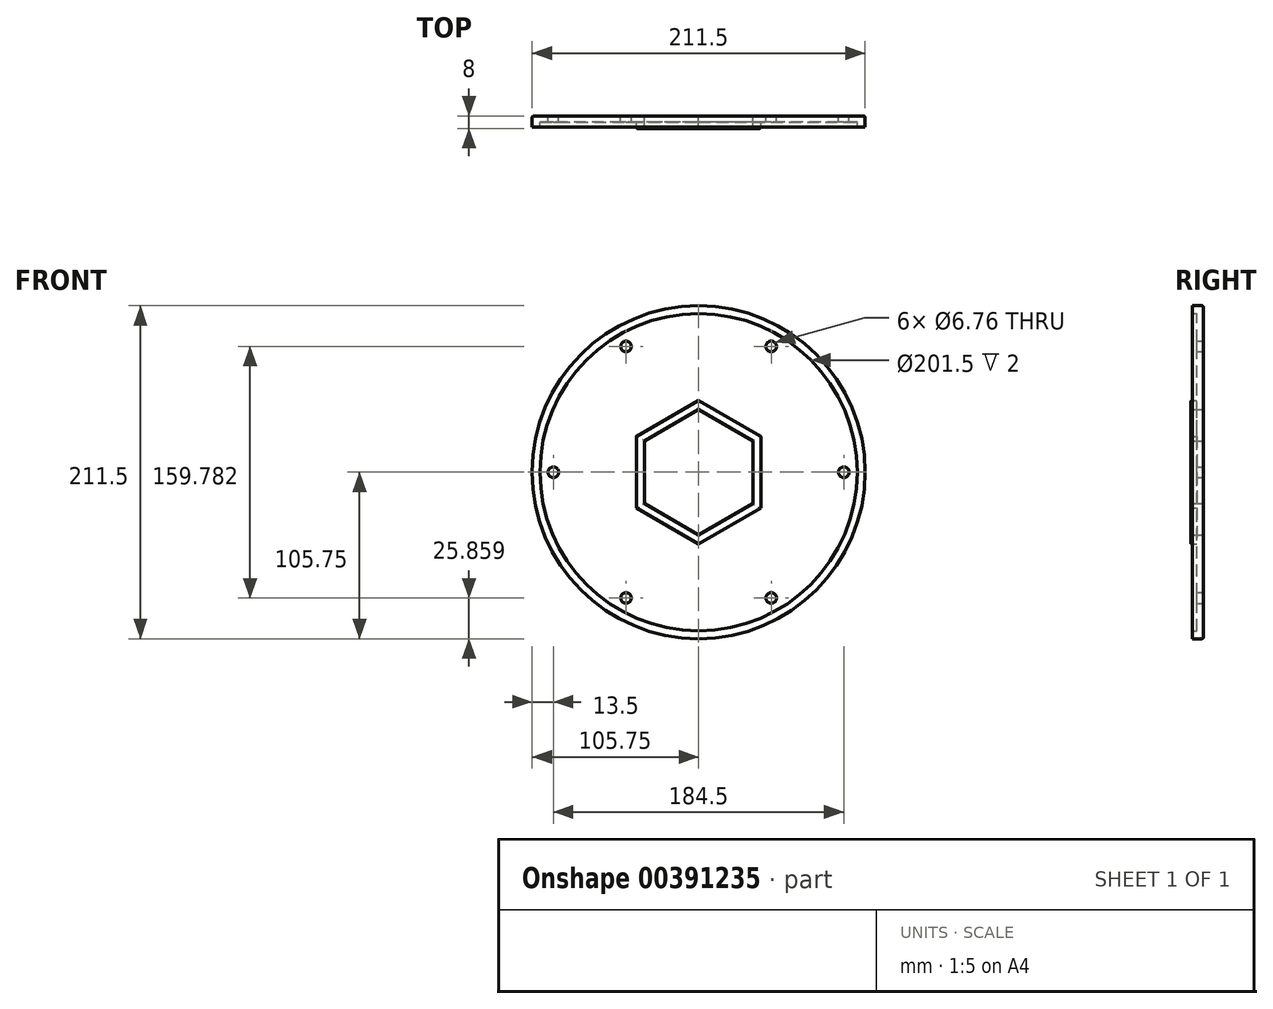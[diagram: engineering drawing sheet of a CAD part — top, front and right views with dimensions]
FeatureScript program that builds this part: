
annotation { "Feature Type Name" : "Feature", "Feature Type Description" : "" }
export const myFeature = defineFeature(function(context is Context, id is Id, definition is map)
    precondition{}
    {
        {
            var Q0;
            Q0=qCreatedBy(makeId("Front.planeOp"),FACE);
            var sketch = newSketch(context, id + "F0", { "sketchPlane" : qUnion([Q0])});
            skCircle(sketch, "E0.cCircle", {"center": v(0, 0) * mm, "radius": 80.5 * mm, "construction": true});
            skLineSegment(sketch, "E0.0", {"start": v(80.5, -46.48) * mm, "end": v(0, -92.95) * mm});
            skLineSegment(sketch, "E0.1", {"start": v(0, -92.95) * mm, "end": v(-80.5, -46.48) * mm});
            skLineSegment(sketch, "E0.2", {"start": v(-80.5, -46.48) * mm, "end": v(-80.5, 46.48) * mm});
            skLineSegment(sketch, "E0.3", {"start": v(-80.5, 46.48) * mm, "end": v(0, 92.95) * mm});
            skLineSegment(sketch, "E0.4", {"start": v(0, 92.95) * mm, "end": v(80.5, 46.48) * mm});
            skLineSegment(sketch, "E0.5", {"start": v(80.5, 46.48) * mm, "end": v(80.5, -46.48) * mm});
            skPoint(sketch, "E0.0.midPoint", {"position": v(40.25, -69.72) * mm});
            skPoint(sketch, "E1.0.midPoint", {"position": v(83.75, 0) * mm});
            skCircle(sketch, "E2", {"center": v(0, 0) * mm, "radius": 100.75 * mm});
            skPoint(sketch, "E3.0.midPoint", {"position": v(19.75, -35.93) * mm});
            skCircle(sketch, "E4.cCircle", {"center": v(0, 0) * mm, "radius": 34.5 * mm, "construction": true});
            skLineSegment(sketch, "E4.0", {"start": v(34.5, -19.92) * mm, "end": v(0, -39.84) * mm});
            skLineSegment(sketch, "E4.1", {"start": v(0, -39.84) * mm, "end": v(-34.5, -19.92) * mm});
            skLineSegment(sketch, "E4.2", {"start": v(-34.5, -19.92) * mm, "end": v(-34.5, 19.92) * mm});
            skLineSegment(sketch, "E4.3", {"start": v(-34.5, 19.92) * mm, "end": v(0, 39.84) * mm});
            skLineSegment(sketch, "E4.4", {"start": v(0, 39.84) * mm, "end": v(34.5, 19.92) * mm});
            skLineSegment(sketch, "E4.5", {"start": v(34.5, 19.92) * mm, "end": v(34.5, -19.92) * mm});
            skPoint(sketch, "E4.0.midPoint", {"position": v(17.25, -29.88) * mm});
            skPoint(sketch, "E5.visualSharp", {"position": v(0, 96.7) * mm});
            skPoint(sketch, "E6.visualSharp", {"position": v(83.75, 48.35) * mm});
            skPoint(sketch, "E7.visualSharp", {"position": v(83.75, -48.35) * mm});
            skPoint(sketch, "E8.visualSharp", {"position": v(0, -96.7) * mm});
            skPoint(sketch, "E9.visualSharp", {"position": v(-83.75, -48.35) * mm});
            skPoint(sketch, "E10.visualSharp", {"position": v(-83.75, 48.35) * mm});
            skPoint(sketch, "E11.visualSharp", {"position": v(39.66, 22.9) * mm});
            skPoint(sketch, "E12.visualSharp", {"position": v(39.58, -24.48) * mm});
            skPoint(sketch, "E13.visualSharp", {"position": v(-0.08, -47.38) * mm});
            skPoint(sketch, "E14.visualSharp", {"position": v(-39.66, -22.9) * mm});
            skPoint(sketch, "E15.visualSharp", {"position": v(-39.66, 22.9) * mm});
            skPoint(sketch, "E16.visualSharp", {"position": v(0, 45.8) * mm});
            skCircle(sketch, "E17.cCircle", {"center": v(0, 0) * mm, "radius": 77.5 * mm, "construction": true});
            skLineSegment(sketch, "E17.0", {"start": v(77.5, 44.74) * mm, "end": v(77.5, -44.74) * mm});
            skLineSegment(sketch, "E17.1", {"start": v(77.5, -44.74) * mm, "end": v(0, -89.49) * mm});
            skLineSegment(sketch, "E17.2", {"start": v(0, -89.49) * mm, "end": v(-77.5, -44.74) * mm});
            skLineSegment(sketch, "E17.3", {"start": v(-77.5, -44.74) * mm, "end": v(-77.5, 44.74) * mm});
            skLineSegment(sketch, "E17.4", {"start": v(-77.5, 44.74) * mm, "end": v(0, 89.49) * mm});
            skLineSegment(sketch, "E17.5", {"start": v(0, 89.49) * mm, "end": v(77.5, 44.74) * mm});
            skPoint(sketch, "E17.0.midPoint", {"position": v(77.5, 0) * mm});
            skCircle(sketch, "E18.cCircle", {"center": v(0, 0) * mm, "radius": 39.5 * mm, "construction": true});
            skLineSegment(sketch, "E18.0", {"start": v(39.5, -22.8) * mm, "end": v(0, -45.61) * mm});
            skLineSegment(sketch, "E18.1", {"start": v(0, -45.61) * mm, "end": v(-39.5, -22.8) * mm});
            skLineSegment(sketch, "E18.2", {"start": v(-39.5, -22.8) * mm, "end": v(-39.5, 22.8) * mm});
            skLineSegment(sketch, "E18.3", {"start": v(-39.5, 22.8) * mm, "end": v(0, 45.61) * mm});
            skLineSegment(sketch, "E18.4", {"start": v(0, 45.61) * mm, "end": v(39.5, 22.8) * mm});
            skLineSegment(sketch, "E18.5", {"start": v(39.5, 22.8) * mm, "end": v(39.5, -22.8) * mm});
            skPoint(sketch, "E18.0.midPoint", {"position": v(19.75, -34.2) * mm});
            skCircle(sketch, "E19", {"center": v(0, 0) * mm, "radius": 105.75 * mm});
            skPoint(sketch, "E20", {"position": v(-46.12, 79.9) * mm});
            skPoint(sketch, "E21", {"position": v(46.12, 79.9) * mm});
            skPoint(sketch, "E22", {"position": v(92.25, 0) * mm});
            skPoint(sketch, "E23", {"position": v(46.13, -79.9) * mm});
            skPoint(sketch, "E24", {"position": v(-46.12, -79.9) * mm});
            skPoint(sketch, "E25", {"position": v(-92.25, 0) * mm});
            skSolve(sketch);
        }
        {
            var Q0;
            Q0=makeQuery(id+"F0.imprint","IMPRINT",FACE,{"disambiguationData":[TD([[makeQuery(id+"F0.imprint","IMPRINT",EDGE,{"derivedFrom":sQuery(id+"F0.wireOp",EDGE,"E0.0")}),1.0]])]});
            var Q1;
            Q1=makeQuery(id+"F0.imprint","IMPRINT",FACE,{"disambiguationData":[TD([[makeQuery(id+"F0.imprint","IMPRINT",EDGE,{"derivedFrom":sQuery(id+"F0.wireOp",EDGE,"E17.0")}),-1.0]])]});
            extrude(context, id + "F1", {"entities" : qUnion([Q0, Q1]), "depth" : 4 * mm});
        }
        {
            var Q0;
            Q0=makeQuery(id+"F0.imprint","IMPRINT",FACE,{"disambiguationData":[TD([[makeQuery(id+"F0.imprint","IMPRINT",EDGE,{"derivedFrom":sQuery(id+"F0.wireOp",EDGE,"E0.0")}),-1.0]])]});
            extrude(context, id + "F2", {"entities" : qUnion([Q0]), "depth" : 4 * mm});
        }
        {
            var Q0;
            Q0=makeQuery(id+"F0.imprint","IMPRINT",FACE,{"disambiguationData":[TD([[makeQuery(id+"F0.imprint","IMPRINT",EDGE,{"derivedFrom":sQuery(id+"F0.wireOp",EDGE,"E4.0")}),1.0]])]});
            extrude(context, id + "F3", {"entities" : qUnion([Q0]), "operationType" : NewBodyOperationType.ADD, "depth" : 8 * mm});
        }
        {
            var Q0;
            Q0=makeQuery(id+"F0.imprint","IMPRINT",FACE,{"disambiguationData":[TD([[makeQuery(id+"F0.imprint","IMPRINT",EDGE,{"derivedFrom":sQuery(id+"F0.wireOp",EDGE,"E2")}),-1.0]])]});
            extrude(context, id + "F4", {"entities" : qUnion([Q0]), "operationType" : NewBodyOperationType.ADD, "depth" : 7 * mm});
        }
        {
            var Q0;
            Q0=makeQuery(id+"F1.opExtrude","SWEPT_BODY",BODY,{"disambiguationData":[OSD([sQuery(id+"F0.wireOp",EDGE,"E0.0"),sQuery(id+"F0.wireOp",EDGE,"E0.1"),sQuery(id+"F0.wireOp",EDGE,"E0.2"),sQuery(id+"F0.wireOp",EDGE,"E0.3"),sQuery(id+"F0.wireOp",EDGE,"E0.4"),sQuery(id+"F0.wireOp",EDGE,"E0.5"),sQuery(id+"F0.wireOp",EDGE,"E2")])]});
            var Q1;
            Q1=makeQuery(id+"F1.opExtrude","SWEPT_BODY",BODY,{"disambiguationData":[OSD([sQuery(id+"F0.wireOp",EDGE,"E17.0"),sQuery(id+"F0.wireOp",EDGE,"E17.1"),sQuery(id+"F0.wireOp",EDGE,"E17.2"),sQuery(id+"F0.wireOp",EDGE,"E17.3"),sQuery(id+"F0.wireOp",EDGE,"E17.4"),sQuery(id+"F0.wireOp",EDGE,"E17.5"),sQuery(id+"F0.wireOp",EDGE,"E18.0"),sQuery(id+"F0.wireOp",EDGE,"E18.1"),sQuery(id+"F0.wireOp",EDGE,"E18.2"),sQuery(id+"F0.wireOp",EDGE,"E18.3"),sQuery(id+"F0.wireOp",EDGE,"E18.4"),sQuery(id+"F0.wireOp",EDGE,"E18.5")])]});
            var Q2;
            Q2=makeQuery(id+"F2.opExtrude","SWEPT_BODY",BODY,{"disambiguationData":[OSD([sQuery(id+"F0.wireOp",EDGE,"E0.0"),sQuery(id+"F0.wireOp",EDGE,"E0.1"),sQuery(id+"F0.wireOp",EDGE,"E0.2"),sQuery(id+"F0.wireOp",EDGE,"E0.3"),sQuery(id+"F0.wireOp",EDGE,"E0.4"),sQuery(id+"F0.wireOp",EDGE,"E0.5"),sQuery(id+"F0.wireOp",EDGE,"E17.0"),sQuery(id+"F0.wireOp",EDGE,"E17.1"),sQuery(id+"F0.wireOp",EDGE,"E17.2"),sQuery(id+"F0.wireOp",EDGE,"E17.3"),sQuery(id+"F0.wireOp",EDGE,"E17.4"),sQuery(id+"F0.wireOp",EDGE,"E17.5")])]});
            booleanBodies(context, id + "F5", {"operationType" : BooleanOperationType.UNION, "tools" : qUnion([Q0, Q1, Q2])});
        }
        {
            var Q0;
            Q0=makeQuery(id+"F3.opExtrude","CAP_EDGE",EDGE,{"disambiguationData":[OSD([sQuery(id+"F0.wireOp",EDGE,"E18.4")])],"isStart":false});
            var Q1;
            Q1=makeQuery(id+"F3.opExtrude","CAP_EDGE",EDGE,{"disambiguationData":[OSD([sQuery(id+"F0.wireOp",EDGE,"E18.5")])],"isStart":false});
            var Q2;
            Q2=makeQuery(id+"F3.opExtrude","CAP_EDGE",EDGE,{"disambiguationData":[OSD([sQuery(id+"F0.wireOp",EDGE,"E18.0")])],"isStart":false});
            var Q3;
            Q3=makeQuery(id+"F3.opExtrude","CAP_EDGE",EDGE,{"disambiguationData":[OSD([sQuery(id+"F0.wireOp",EDGE,"E18.1")])],"isStart":false});
            var Q4;
            Q4=makeQuery(id+"F3.opExtrude","CAP_EDGE",EDGE,{"disambiguationData":[OSD([sQuery(id+"F0.wireOp",EDGE,"E18.2")])],"isStart":false});
            var Q5;
            Q5=makeQuery(id+"F3.opExtrude","CAP_EDGE",EDGE,{"disambiguationData":[OSD([sQuery(id+"F0.wireOp",EDGE,"E18.3")])],"isStart":false});
            fillet(context, id + "F6", {"entities" : qUnion([Q0, Q1, Q2, Q3, Q4, Q5]), "radius" : 1 * mm, "tangentPropagation" : true, "allowEdgeOverflow" : false});
        }
        {
            var Q0;
            Q0=makeQuery(id+"F1.opExtrude","CAP_EDGE",EDGE,{"disambiguationData":[OSD([sQuery(id+"F0.wireOp",EDGE,"E2")])],"isStart":false});
            var Q1;
            Q1=makeQuery(id+"F4.opExtrude","CAP_EDGE",EDGE,{"disambiguationData":[OSD([sQuery(id+"F0.wireOp",EDGE,"E19")])],"isStart":true});
            var Q2;
            {var subQ0=sQuery(id+"F0.wireOp",EDGE,"E2");var subQ1=sQuery(id+"F0.wireOp",EDGE,"E0.5");var subQ2=sQuery(id+"F0.wireOp",EDGE,"E0.4");var subQ3=sQuery(id+"F0.wireOp",EDGE,"E0.3");var subQ4=sQuery(id+"F0.wireOp",EDGE,"E0.2");var subQ5=sQuery(id+"F0.wireOp",EDGE,"E0.1");var subQ6=sQuery(id+"F0.wireOp",EDGE,"E0.0");var subQ7=sQuery(id+"F0.wireOp",EDGE,"E18.5");var subQ8=sQuery(id+"F0.wireOp",EDGE,"E18.4");var subQ9=sQuery(id+"F0.wireOp",EDGE,"E18.3");var subQ10=sQuery(id+"F0.wireOp",EDGE,"E18.2");var subQ11=sQuery(id+"F0.wireOp",EDGE,"E18.1");var subQ12=sQuery(id+"F0.wireOp",EDGE,"E18.0");var subQ13=sQuery(id+"F0.wireOp",EDGE,"E17.5");var subQ14=sQuery(id+"F0.wireOp",EDGE,"E17.4");var subQ15=sQuery(id+"F0.wireOp",EDGE,"E17.3");var subQ16=sQuery(id+"F0.wireOp",EDGE,"E17.2");var subQ17=sQuery(id+"F0.wireOp",EDGE,"E17.1");var subQ18=sQuery(id+"F0.wireOp",EDGE,"E17.0");Q2=makeQuery(id+"F5.opBoolean","MERGE",FACE,{"derivedFrom":[makeQuery(id+"F2.opExtrude","CAP_FACE",FACE,{"disambiguationData":[OSD([subQ6,subQ5,subQ4,subQ3,subQ2,subQ1,subQ18,subQ17,subQ16,subQ15,subQ14,subQ13])],"isStart":true}),makeQuery(id+"F3.boolean.opBoolean","MERGE",FACE,{"derivedFrom":[makeQuery(id+"F1.opExtrude","CAP_FACE",FACE,{"disambiguationData":[OSD([subQ18,subQ17,subQ16,subQ15,subQ14,subQ13,subQ12,subQ11,subQ10,subQ9,subQ8,subQ7])],"isStart":true}),makeQuery(id+"F3.opExtrude","CAP_FACE",FACE,{"disambiguationData":[OSD([sQuery(id+"F0.wireOp",EDGE,"E4.0"),sQuery(id+"F0.wireOp",EDGE,"E4.1"),sQuery(id+"F0.wireOp",EDGE,"E4.2"),sQuery(id+"F0.wireOp",EDGE,"E4.3"),sQuery(id+"F0.wireOp",EDGE,"E4.4"),sQuery(id+"F0.wireOp",EDGE,"E4.5"),subQ12,subQ11,subQ10,subQ9,subQ8,subQ7])],"isStart":true})]}),makeQuery(id+"F4.boolean.opBoolean","MERGE",FACE,{"derivedFrom":[makeQuery(id+"F1.opExtrude","CAP_FACE",FACE,{"disambiguationData":[OSD([subQ6,subQ5,subQ4,subQ3,subQ2,subQ1,subQ0])],"isStart":true}),makeQuery(id+"F4.opExtrude","CAP_FACE",FACE,{"disambiguationData":[OSD([subQ0,sQuery(id+"F0.wireOp",EDGE,"E19")])],"isStart":true})]})]});}
            fillet(context, id + "F7", {"entities" : qUnion([Q0, Q1, Q2]), "radius" : 1 * mm, "tangentPropagation" : true, "allowEdgeOverflow" : false});
        }
        {
            var Q0;
            Q0=sQuery(id+"F0.wireOp",VERTEX,"E20");
            var Q1;
            Q1=sQuery(id+"F0.wireOp",VERTEX,"E21");
            var Q2;
            Q2=sQuery(id+"F0.wireOp",VERTEX,"E22");
            var Q3;
            Q3=sQuery(id+"F0.wireOp",VERTEX,"E23");
            var Q4;
            Q4=sQuery(id+"F0.wireOp",VERTEX,"E24");
            var Q5;
            Q5=sQuery(id+"F0.wireOp",VERTEX,"E25");
            var Q6;
            Q6=makeQuery(id+"F1.opExtrude","SWEPT_BODY",BODY,{"disambiguationData":[OSD([sQuery(id+"F0.wireOp",EDGE,"E0.0"),sQuery(id+"F0.wireOp",EDGE,"E0.1"),sQuery(id+"F0.wireOp",EDGE,"E0.2"),sQuery(id+"F0.wireOp",EDGE,"E0.3"),sQuery(id+"F0.wireOp",EDGE,"E0.4"),sQuery(id+"F0.wireOp",EDGE,"E0.5"),sQuery(id+"F0.wireOp",EDGE,"E2")])]});
            hole(context, id + "F8", {"style" : HoleStyle.SIMPLE, "endStyle" : HoleEndStyle.THROUGH, "oppositeDirection" : true, "standardTappedOrClearance" : lookupTablePath({ "standard" : "ANSI", "fit" : "Normal (ASME)", "size" : "1/4", "type" : "Clearance" }), "standardBlindInLast" : lookupTablePath({ "fit" : "Free", "standard" : "ANSI", "size" : "1/4", "type" : "Clearance" }), "holeDiameter" : 6.76 * mm, "tappedDepth" : 12 * mm, "tapClearance" : 3, "locations" : qUnion([Q0, Q1, Q2, Q3, Q4, Q5]), "scope" : qUnion([Q6])});
        }
        {
            var Q0;
            Q0=makeQuery(id+"F4.opExtrude","CAP_EDGE",EDGE,{"disambiguationData":[OSD([sQuery(id+"F0.wireOp",EDGE,"E2")])],"isStart":false});
            fillet(context, id + "F9", {"entities" : qUnion([Q0]), "radius" : 1 * mm, "tangentPropagation" : true, "allowEdgeOverflow" : false});
        }
    });
